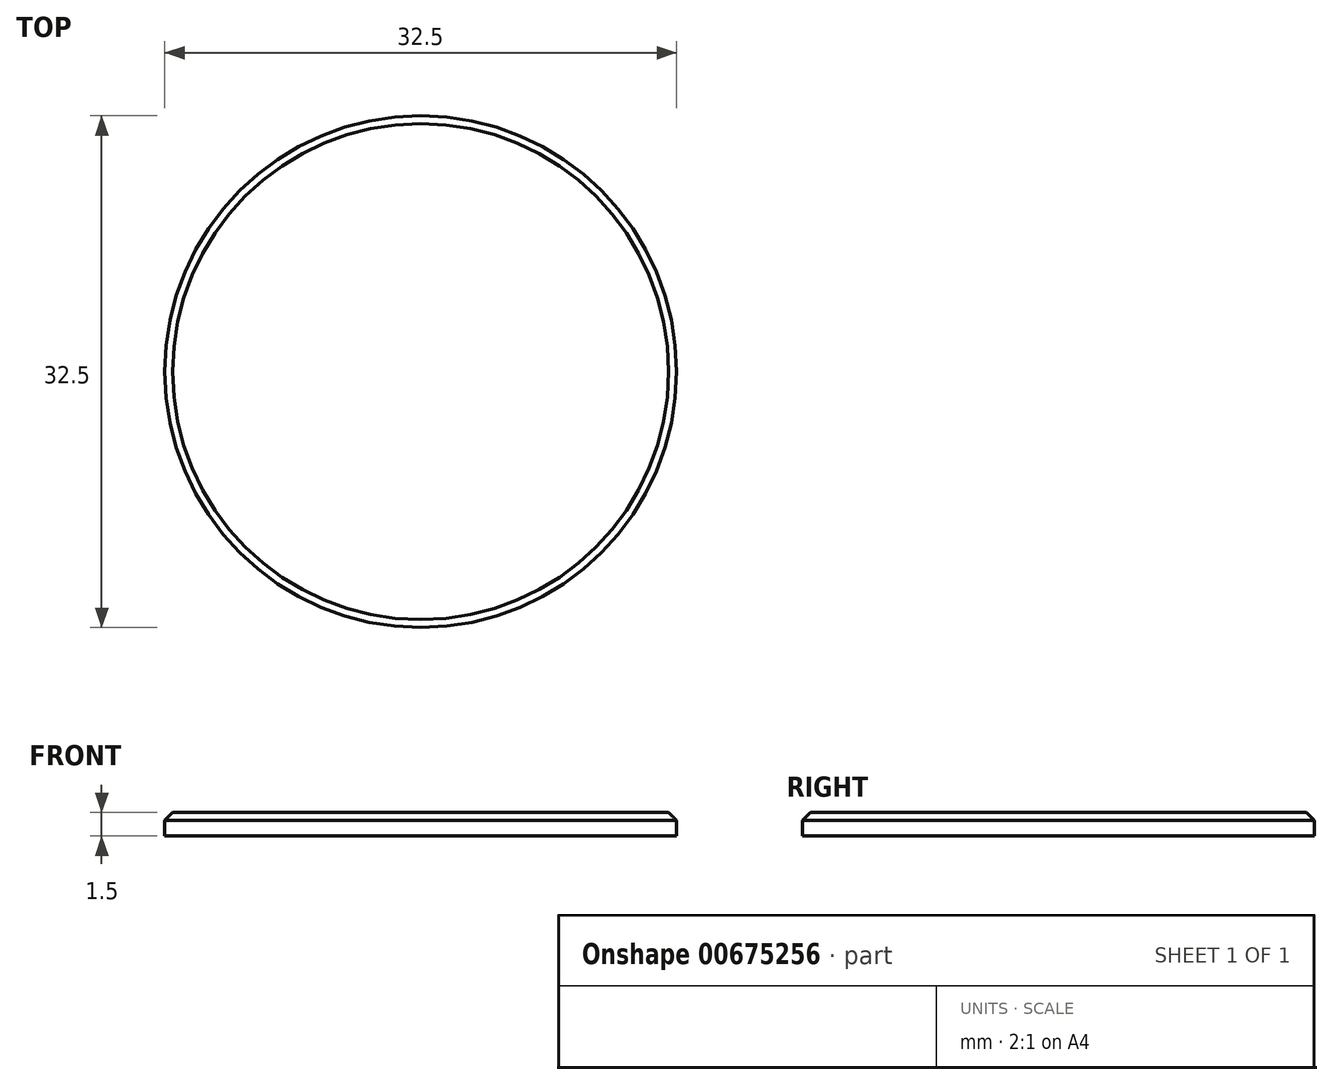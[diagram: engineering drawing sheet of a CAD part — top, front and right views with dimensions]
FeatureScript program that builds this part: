
annotation { "Feature Type Name" : "Feature", "Feature Type Description" : "" }
export const myFeature = defineFeature(function(context is Context, id is Id, definition is map)
    precondition{}
    {
        {
            var Q0;
            Q0=qCreatedBy(makeId("Top.planeOp"),FACE);
            var sketch = newSketch(context, id + "F0", { "sketchPlane" : qUnion([Q0])});
            skCircle(sketch, "E0", {"center": v(0, 0) * mm, "radius": 16.25 * mm});
            skSolve(sketch);
        }
        {
            var Q0;
            Q0=makeQuery(id+"F0.imprint","IMPRINT",FACE,{"disambiguationData":[TD([[makeQuery(id+"F0.imprint","IMPRINT",EDGE,{"derivedFrom":sQuery(id+"F0.wireOp",EDGE,"E0")}),1.0]])]});
            extrude(context, id + "F1", {"entities" : qUnion([Q0]), "depth" : 1.5 * mm, "offsetDistance" : 25 * mm});
        }
        {
            var Q0;
            Q0=qCreatedBy(makeId("Top.planeOp"),FACE);
            cPlane(context, id + "F2", {"entities" : qUnion([Q0]), "cplaneType" : CPlaneType.OFFSET, "offset" : 3 * mm, "width" : 150 * mm, "height" : 150 * mm});
        }
        {
            var Q0;
            Q0=makeQuery(id+"F1.opExtrude","CAP_FACE",FACE,{"disambiguationData":[OSD([sQuery(id+"F0.wireOp",EDGE,"E0")])],"isStart":false});
            chamfer(context, id + "F3", {"entities" : qUnion([Q0]), "width" : .5 * mm, "tangentPropagation" : true});
        }
    });
